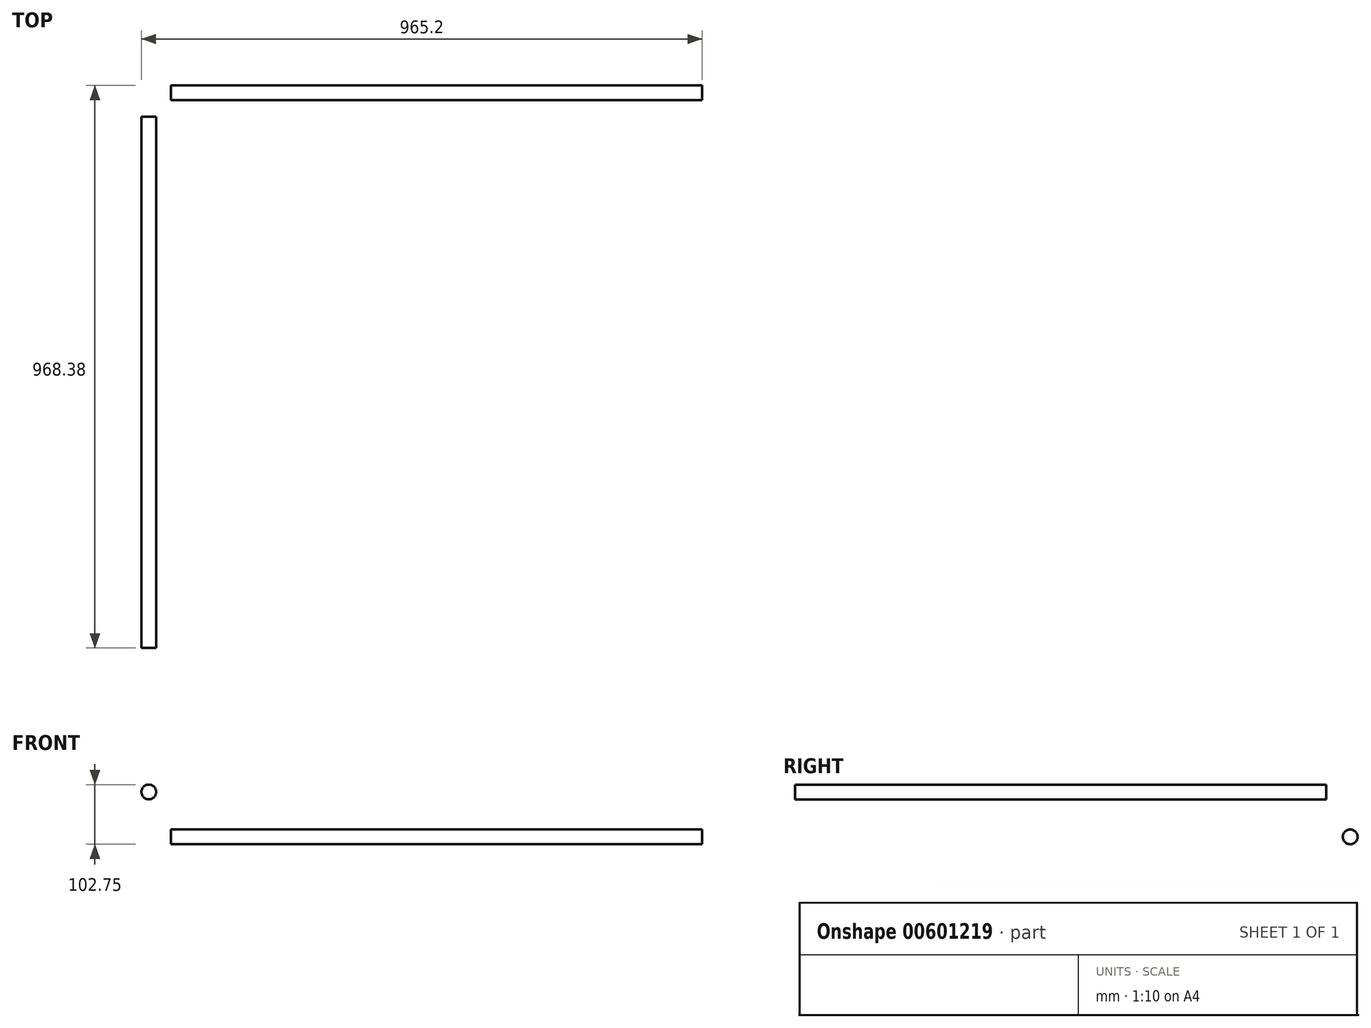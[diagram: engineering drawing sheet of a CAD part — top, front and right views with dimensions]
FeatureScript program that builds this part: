
annotation { "Feature Type Name" : "Feature", "Feature Type Description" : "" }
export const myFeature = defineFeature(function(context is Context, id is Id, definition is map)
    precondition{}
    {
        {
            var Q0;
            Q0=qCreatedBy(makeId("Front.planeOp"),FACE);
            var sketch = newSketch(context, id + "F0", { "sketchPlane" : qUnion([Q0])});
            skCircle(sketch, "E0", {"center": v(-38.1, 26.1) * mm, "radius": 12.7 * mm});
            skSolve(sketch);
        }
        {
            var Q0;
            Q0 = qSketchRegion(id + "F0", true);
            extrude(context, id + "F1", {"entities" : qUnion([Q0]), "depth" : 914.4 * mm, "offsetDistance" : 25.4 * mm});
        }
        {
            var Q0;
            Q0=qCreatedBy(makeId("Right.planeOp"),FACE);
            var sketch = newSketch(context, id + "F2", { "sketchPlane" : qUnion([Q0])});
            skCircle(sketch, "E1", {"center": v(41.28, -51.24) * mm, "radius": 12.7 * mm});
            skSolve(sketch);
        }
        {
            var Q0;
            Q0 = qSketchRegion(id + "F2", true);
            extrude(context, id + "F3", {"entities" : qUnion([Q0]), "depth" : 914.4 * mm, "offsetDistance" : 25.4 * mm});
        }
    });
